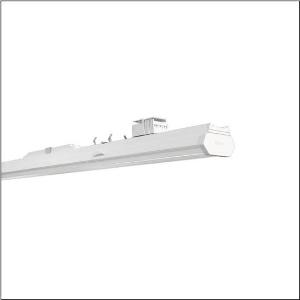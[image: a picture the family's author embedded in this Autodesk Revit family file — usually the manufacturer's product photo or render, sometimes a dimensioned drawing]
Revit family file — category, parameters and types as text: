
# Revit family: licross_r__21_protected_mo_52td12cn49xg_6de8
name_source: partatom
category: Lighting Fixtures
units: mm (PartAtom-declared; Revit-internal decimal feet)

## family parameters
Cut with Voids When Loaded = No
Host = Face
Light Source = No
Part Type = Normal
Room Calculation Point = No
Round Connector Dimension = Use Diameter
Shared = No

## types (1)
- --- (1 x LED, 9110 lm, 50.4 W, 4000K)
    Apparent Load = 50 VA
    CIE Flux Codes = 73 92 98 99 100
    Color Rendering = 80
    Color Temperature = 4000K
    Default Elevation = 1800 mm
    Description = Licross® 21 Protected MO, luminaire insert, of sheet steel, galvanised, coil coated, white, length: 1.500mm, width: 90mm, height: 103mm, LED rated luminous flux: 9.120lm, light colour: 840, control gear: ON/OFF Multilumen, CLOi, control gear: ECG Multilumen, with plug, 3-pole, with phase selection, mains connection: 220..240V, AC, 50/60Hz, start of lifetime: 50W, end of service life: 61W, halogen-free wiring, primary light control with lens, of plastic, primary optical cover: cover, of PMMA, light emission: direct distribution, primary light characteristic: symmetric, protection rating (complete): IP54, insulation class (complete): insulation class I (protective earthing), certification: CE, ENEC, VDE, UKCA, protection symbol: D if used in an environment with non-conductive dust loads with corresponding accessories, impact resistance: IK06, permissible ambient temperature for indoor applications: -35..+45°C, corresponds to IFS (International Featured Standards) requirements for safety and quality in the food industry, reducing of maximum allowable ambient temperature of 5°C with ceiling mounting, LABS conformity tested according to VDMA 24364:2018-05, packaging unit: 1 piece
    Height = 92 mm
    Lamp = 1 x LED
    Lamp Light Flux = 9110 lm
    Lamp Power = 50.4 W
    Lamp count = 1
    Length = 1500 mm
    Luminous efficacy = 181 lm/W
    Manufacturer = Siteco
    ModVariant = No
    Model = 52TD12CN49XG
    Mounting Place = Ceiling
    Mounting Type = Pendant
    Number of Poles = 1
    OnlyDefault = Yes
    Power Factor = 1
    Product Name = Licross® 21 Protected MO
    Product group = luminaire insert
    ProductGroupID = 901
    Protection Class = Protection class I
    Protection Degree = IP 54
    RLX_Detail_Level = 1
    RLX_Emergency_Light_Flux = 0 lm
    RLX_Emergency_Type = 0
    RLX_Emergency_Type_DB = No
    RlxData = <blob elided: 22213 chars, md5=f491fe1a>
    Socket = socket
    Standby Power = 0 W
    System Light Flux = 9110 lm
    System Power = 50 W
    Type Comments = factory setting: luminous flux: 100 % | (A | C | E) | 117 mA
    Type Image = l_1256148.jpg
    URL = http://relux.com
    VarID = @adj_041289
    Voltage = 0 V
    Weight = 0.00 kg
    Width = 88 mm

## geometry (parser evidence)
native form markers: Blend x4, Sweep x12
no freeform markers — native parametric forms only
